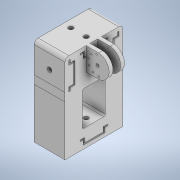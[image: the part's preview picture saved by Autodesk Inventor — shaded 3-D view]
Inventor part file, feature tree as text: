
AUTODESK INVENTOR PART (.ipt)
format: ipt  version: 2021 (Build 250183000, 183)  size: 340,480 bytes
history: native  units: mm
features: extrude x7, sketch x7, other x3, fillet x1
ambient origin geometry x8: Origin, YZ Plane, XZ Plane, XY Plane, X Axis, Y Axis, Z Axis, Center Point
bodies: Solid1 (feature_tree)
feature tree (18):
  other  "din_connector.ipt"
  extrude  "Extrusion1"  Depth=10.0mm TaperAngle=0.0deg
  extrude  "Extrusion2"  Depth=30.0mm TaperAngle=0.0deg
  extrude  "Extrusion3"  Depth=30.0mm TaperAngle=0.0deg
  extrude  "Extrusion4"  Depth=4.0mm
  extrude  "Extrusion5"  Depth=5.0mm
  extrude  "Extrusion6"  Depth=5.0mm
  extrude  "Extrusion7"  Depth=10.0mm
  fillet  "Fillet1"  Radius=45.0mm
  other  "Solid1::din_connector.ipt"
  other  "TaggingFeature1"
  sketch  "Sketch1"  dims[d0=10.0mm d1=10.0mm d2=0.0mm]
  sketch  "Sketch2"  dims[d6=29.862mm d7=0.0mm d8=30.0mm d9=0.0mm]
  sketch  "Sketch3"  dims[d11=2.0mm d16=30.0mm d17=0.0mm]
  sketch  "Sketch4"  dims[d18=60.0mm d20=180.0deg d22=4.0mm]
  sketch  "Sketch5"  dims[d23=30.0mm d24=0.0mm d25=5.0mm]
  sketch  "Sketch6"  dims[d26=10.0mm d27=5.0mm]
  sketch  "Sketch7"  dims[d28=10.0mm d29=0.0mm d30=10.0mm d31=45.0mm d32=10.0mm d33=10.0mm d34=10.0mm d35=0.0mm d36=2.0mm]
